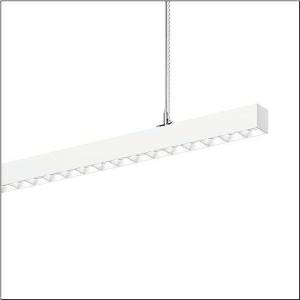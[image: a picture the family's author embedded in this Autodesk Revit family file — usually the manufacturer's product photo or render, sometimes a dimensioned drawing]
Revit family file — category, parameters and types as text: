
# Revit family: silica_r__21_51mx35da47wb_183f
name_source: partatom
category: Lighting Fixtures
units: mm (PartAtom-declared; Revit-internal decimal feet)

## family parameters
Cut with Voids When Loaded = No
Host = Face
Light Source = No
Part Type = Normal
Room Calculation Point = No
Round Connector Dimension = Use Diameter
Shared = No

## types (1)
- --- (1 x LED, 7080 lm, 40.6 W, 4000K)
    Apparent Load = 41 VA
    CIE Flux Codes = 84 98 100 61 100
    Color Rendering = 80
    Color Temperature = 4000K
    Default Elevation = 1800 mm
    Description = Silica® 21, office luminaire, primary light control with darklight reflector, of PMMA, white, CAT 2 (L<= 3000cd/m²), light emission: direct/indirect distribution, primary light characteristic: symmetric, installation type: suspended mounting, LED, rated luminous flux: 7.080lm, luminous efficacy: 174lm/W, light colour: 840, colour temperature: 4000K, control gear: DALI 2, with terminal, 3+2-pole, max. 2.5mm², mains connection: 220..240V, AC, 50/60Hz, rated input power: 40.6W, luminaire housing, of aluminium, traffic white (RAL 9016), length: 1.204mm, width: 53mm, height: 53mm, protection rating (complete): IP20, insulation class (complete): insulation class I (protective earthing), certification: CE, permissible operating ambient temperature: 0..+35°C, standard: EN 50419, packaging unit: 1 piece
    Height = 53 mm
    Lamp = 1 x LED
    Lamp Light Flux = 7080 lm
    Lamp Power = 40.6 W
    Lamp count = 1
    Length = 1204 mm
    Luminous efficacy = 174 lm/W
    Manufacturer = Siteco
    ModVariant = No
    Model = 51MX35DA47WB
    Mounting Place = Ceiling
    Mounting Type = Pendant
    Number of Poles = 1
    OnlyDefault = Yes
    Power Factor = 1
    Product Name = Silica® 21
    Product group = office luminaire | ceiling pendant
    ProductGroupID = 904
    Protection Class = Protection class I
    Protection Degree = IP 20
    RLX_Detail_Level = 1
    RLX_Emergency_Light_Flux = 0 lm
    RLX_Emergency_Type = 0
    RLX_Emergency_Type_DB = No
    RlxData = <blob elided: 40997 chars, md5=43fe38e7>
    Socket = socket
    Standby Power = 0 W
    System Light Flux = 7080 lm
    System Power = 41 W
    Type Comments = factory setting: luminous flux: 100 % | dim-lin: 254 | 339 mA
    Type Image = l_1335921.jpg
    URL = http://relux.com
    VarID = @adj_120514
    Voltage = 0 V
    Weight = 0.00 kg
    Width = 53 mm

## geometry (parser evidence)
native form markers: Blend x4, Sweep x11
no freeform markers — native parametric forms only
